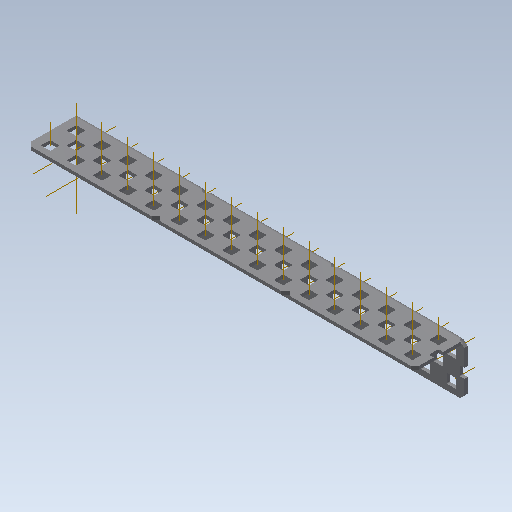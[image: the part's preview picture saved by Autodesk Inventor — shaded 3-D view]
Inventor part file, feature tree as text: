
AUTODESK INVENTOR PART (.ipt)
format: ipt  version: 2020 (Build 240168000, 168)  size: 2,040,832 bytes
history: native  units: in
note: dims shown in document units (in); Inventor stores cm internally (conversion verified against a paired STEP export)
features: other x95, pattern_linear x4, sheet_metal_op x1, extrude x1, imported_body x1, sketch x1
ambient origin geometry x8: Origin, YZ Plane, XZ Plane, XY Plane, X Axis, Y Axis, Z Axis, Center Point
bodies: Body1 (feature_tree)
feature tree (103):
  sheet_metal_op  "Fold1"
  other  "L-Channel"
  extrude  "length cut"  Depth=0.5in
  other  "top out axis"
  other  "top inner axis"
  other  "back out axis"
  other  "back inner axis"
  pattern_linear  "top outer axes"  Count1=2 Spacing1=0.5in
  pattern_linear  "top inner axes"  Spacing1=0.5in  [1 undecoded]
  pattern_linear  "back outer axes"  Count1=2 Spacing1=0.5in
  pattern_linear  "back inner axes"  Spacing1=0.5in  [1 undecoded]
  other  "right plane"
  imported_body  "Base1"
  sketch  "Sketch1"  dims[d1=0.0in d4=0.5in d5=0.7874in d7=0.5in d10=0.5in d13=0.5in d14=0.7874in d16=0.5in d19=0.5in d20=-7.5in d21=0.0in d22=0.0in d23=0.0in d24=0.0in d25=0.0in d26=0.0in]
  other  "Work Point1"
  other  "Work Point2"
  other  "Work Point3"
  other  "Work Point4"
  other  "Work Axis5"
  other  "Work Axis6"
  other  "Work Axis7"
  other  "Work Axis8"
  other  "Work Axis11"
  other  "Work Axis12"
  other  "Work Axis13"
  other  "Work Axis14"
  other  "Work Axis15"
  other  "Work Axis18"
  other  "Work Axis19"
  other  "Work Axis20"
  other  "Work Axis23"
  other  "Work Axis24"
  other  "Work Axis25"
  other  "Work Axis26"
  other  "Work Axis29"
  other  "Work Axis30"
  other  "Work Axis31"
  other  "Work Axis32"
  other  "Work Axis33"
  other  "Work Axis36"
  other  "Work Axis37"
  other  "Work Axis38"
  other  "Work Axis41"
  other  "Work Axis42"
  other  "Work Axis43"
  other  "Work Axis44"
  other  "Work Axis45"
  other  "Work Axis61"
  other  "Work Axis62"
  other  "Work Axis63"
  other  "Work Axis64"
  other  "Work Axis65"
  other  "Work Axis81"
  other  "Work Axis82"
  other  "Work Axis83"
  other  "Work Axis84"
  other  "Work Axis85"
  other  "Work Axis101"
  other  "Work Axis102"
  other  "Work Axis103"
  other  "Work Axis104"
  other  "Work Axis105"
  other  "Work Axis121"
  other  "Work Axis122"
  other  "Work Axis123"
  other  "Work Axis124"
  other  "Work Axis125"
  other  "Work Axis141"
  other  "Work Axis142"
  other  "Work Axis143"
  other  "Work Axis144"
  other  "Work Axis145"
  other  "left plane"
  other  "Work Axis161"
  other  "Work Axis162"
  other  "Work Axis163"
  other  "Work Axis164"
  other  "Work Axis165"
  other  "Work Axis166"
  other  "Work Axis167"
  other  "Work Axis168"
  other  "Work Axis169"
  other  "Work Axis170"
  other  "Work Axis171"
  other  "Work Axis172"
  other  "Work Axis173"
  other  "Work Axis174"
  other  "Work Axis175"
  other  "Work Axis176"
  other  "Work Axis177"
  other  "Work Axis178"
  other  "Work Axis179"
  other  "Work Axis180"
  other  "Work Axis181"
  other  "Work Axis182"
  other  "Work Axis183"
  other  "Work Axis184"
  other  "Work Axis185"
  other  "Work Axis186"
  other  "Work Axis187"
  other  "Work Axis188"
  other  "Work Axis189"
  other  "Work Axis190"
note: 2 required parameter values undecoded (feature->parameter linkage not recoverable at this tier; creation-order binding heuristic only, values carry confidence <= 0.55)
